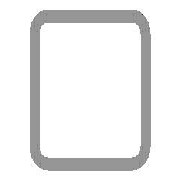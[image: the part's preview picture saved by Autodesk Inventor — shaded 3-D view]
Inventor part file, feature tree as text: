
AUTODESK INVENTOR PART (.ipt)
format: ipt  version: 2025 (Build 290162010, 162A)  size: 133,632 bytes
history: native  units: mm (DEFAULTED — no unit token found)
features: other x4, sketch x1, plane x1
ambient origin geometry x8: Origin, YZ Plane, XZ Plane, XY Plane, X Axis, Y Axis, Z Axis, Center Point
bodies: Solid1 (feature_tree), Body (feature_tree)
feature tree (6):
  parser-record x1  (decoder bookkeeping rows leaked as tree rows — omitted from the tree; the rows remain in map.json)
  other  "Driven Length"
  other  "Start Plane"
  other  "End Plane"
  sketch  "Sketch3"  dims[d3=550.0mm d4=0.0mm d7=8.0mm d9=100.0mm d11=100.0mm d12=4.0mm d13=100.0mm d14=650.0mm d15=50.0mm d16=50.0mm d17=90.0deg d18=550.0mm]
  plane  "Work Plane3"
